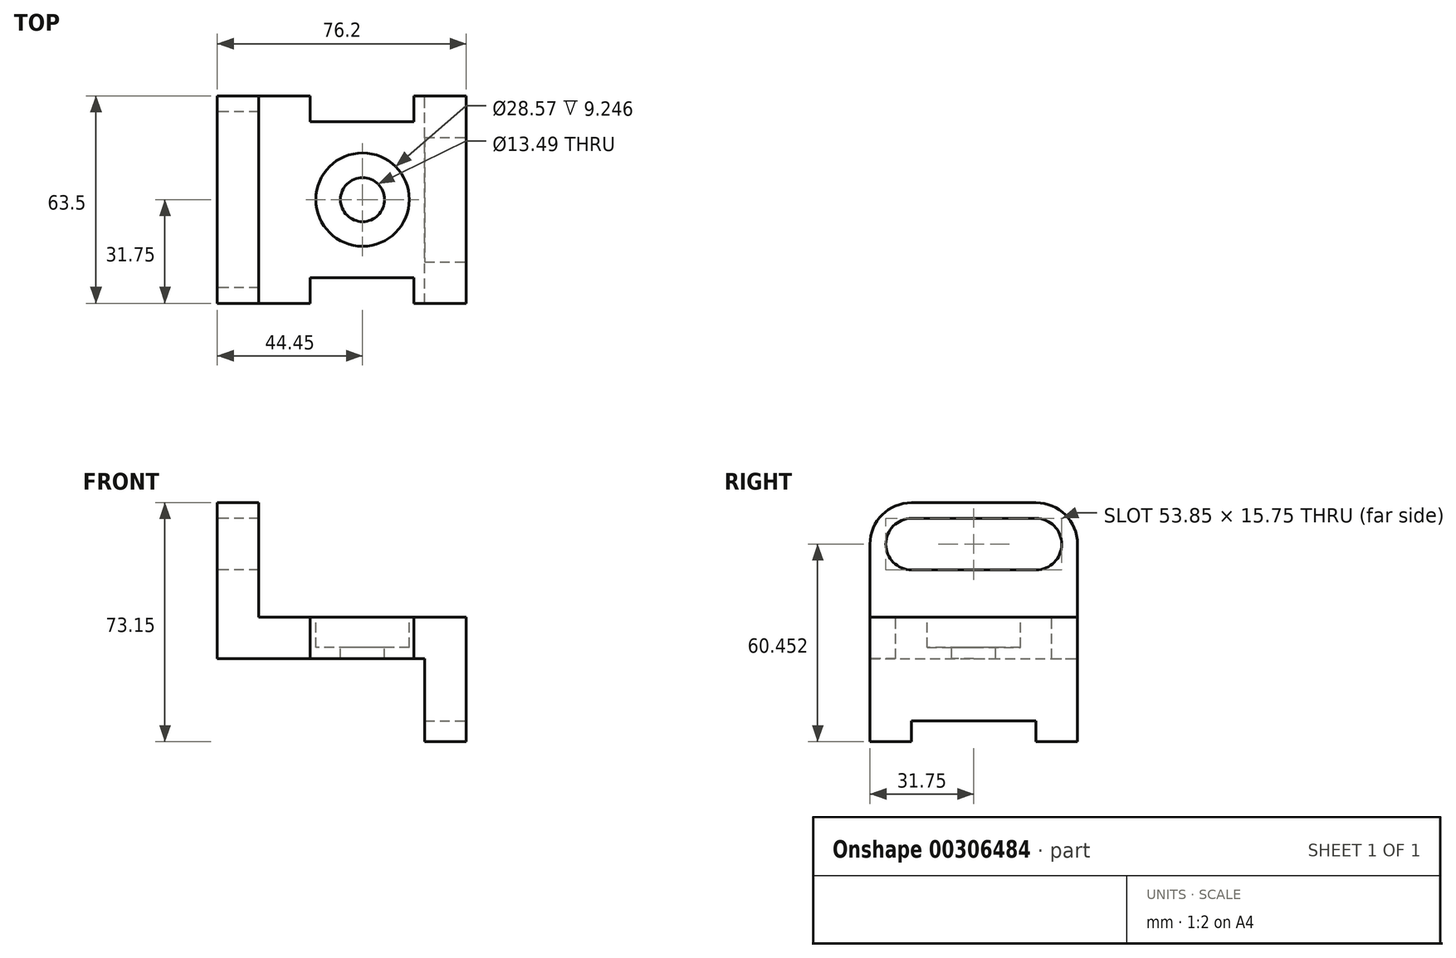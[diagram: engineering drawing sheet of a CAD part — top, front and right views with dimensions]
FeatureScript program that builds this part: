
annotation { "Feature Type Name" : "Feature", "Feature Type Description" : "" }
export const myFeature = defineFeature(function(context is Context, id is Id, definition is map)
    precondition{}
    {
        {
            var Q0;
            Q0=qCreatedBy(makeId("Front.planeOp"),FACE);
            var sketch = newSketch(context, id + "F0", { "sketchPlane" : qUnion([Q0])});
            skLineSegment(sketch, "E0", {"start": v(0, 12.7) * mm, "end": v(76.2, 12.7) * mm});
            skLineSegment(sketch, "E1", {"start": v(76.2, 12.7) * mm, "end": v(76.2, -25.4) * mm});
            skLineSegment(sketch, "E2", {"start": v(76.2, -25.4) * mm, "end": v(63.5, -25.4) * mm});
            skLineSegment(sketch, "E3", {"start": v(63.5, -25.4) * mm, "end": v(63.5, 0) * mm});
            skLineSegment(sketch, "E4", {"start": v(63.5, 0) * mm, "end": v(0, 0) * mm});
            skLineSegment(sketch, "E5", {"start": v(0, 12.7) * mm, "end": v(0, 0) * mm});
            skSolve(sketch);
        }
        {
            var Q0;
            Q0 = qSketchRegion(id + "F0", true);
            extrude(context, id + "F1", {"entities" : qUnion([Q0]), "depth" : 63.5 * mm});
        }
        {
            var Q0;
            Q0=makeQuery(id+"F1.opExtrude","SWEPT_FACE",FACE,{"disambiguationData":[OSD([sQuery(id+"F0.wireOp",EDGE,"E0")])]});
            var sketch = newSketch(context, id + "F2", { "sketchPlane" : qUnion([Q0])});
            skLineSegment(sketch, "E6.bottom", {"start": v(28.45, -63.5) * mm, "end": v(60.2, -63.5) * mm});
            skLineSegment(sketch, "E6.top", {"start": v(28.45, -55.63) * mm, "end": v(60.2, -55.63) * mm});
            skLineSegment(sketch, "E6.left", {"start": v(28.45, -63.5) * mm, "end": v(28.45, -55.63) * mm});
            skLineSegment(sketch, "E6.right", {"start": v(60.2, -63.5) * mm, "end": v(60.2, -55.63) * mm});
            skLineSegment(sketch, "E7.bottom", {"start": v(28.45, 0) * mm, "end": v(60.2, 0) * mm});
            skLineSegment(sketch, "E7.top", {"start": v(28.45, -7.87) * mm, "end": v(60.2, -7.87) * mm});
            skLineSegment(sketch, "E7.left", {"start": v(28.45, 0) * mm, "end": v(28.45, -7.87) * mm});
            skLineSegment(sketch, "E7.right", {"start": v(60.2, 0) * mm, "end": v(60.2, -7.87) * mm});
            skSolve(sketch);
        }
        {
            var Q0;
            Q0 = qSketchRegion(id + "F2", true);
            extrude(context, id + "F3", {"entities" : qUnion([Q0]), "operationType" : NewBodyOperationType.REMOVE, "endBound" : BoundingType.THROUGH_ALL, "oppositeDirection" : true, "depth" : 25.4 * mm});
        }
        {
            var Q0;
            Q0=makeQuery(id+"F1.opExtrude","SWEPT_FACE",FACE,{"disambiguationData":[OSD([sQuery(id+"F0.wireOp",EDGE,"E1")])]});
            var sketch = newSketch(context, id + "F4", { "sketchPlane" : qUnion([Q0])});
            skLineSegment(sketch, "E8.bottom", {"start": v(-50.8, -25.4) * mm, "end": v(-12.7, -25.4) * mm});
            skLineSegment(sketch, "E8.top", {"start": v(-50.8, -19.05) * mm, "end": v(-12.7, -19.05) * mm});
            skLineSegment(sketch, "E8.left", {"start": v(-50.8, -25.4) * mm, "end": v(-50.8, -19.05) * mm});
            skLineSegment(sketch, "E8.right", {"start": v(-12.7, -25.4) * mm, "end": v(-12.7, -19.05) * mm});
            skSolve(sketch);
        }
        {
            var Q0;
            Q0=makeQuery(id+"F4.imprint","IMPRINT",FACE,{"disambiguationData":[TD([[makeQuery(id+"F4.imprint","IMPRINT",EDGE,{"derivedFrom":sQuery(id+"F4.wireOp",EDGE,"E8.bottom")}),1.0]])]});
            extrude(context, id + "F5", {"entities" : qUnion([Q0]), "operationType" : NewBodyOperationType.REMOVE, "endBound" : BoundingType.THROUGH_ALL, "oppositeDirection" : true, "depth" : 25.4 * mm});
        }
        {
            var Q0;
            Q0=qCreatedBy(makeId("Right.planeOp"),FACE);
            var sketch = newSketch(context, id + "F6", { "sketchPlane" : qUnion([Q0])});
            skLineSegment(sketch, "E9", {"start": v(-63.5, 12.7) * mm, "end": v(-63.5, 35.05) * mm});
            skArc(sketch, "E10", {"start": v(-50.8, 47.75) * mm, "mid": v(-59.78, 44.03) * mm, "end": v(-63.5, 35.05) * mm});
            skLineSegment(sketch, "E11", {"start": v(-50.8, 47.75) * mm, "end": v(-31.75, 47.75) * mm});
            skLineSegment(sketch, "E12", {"start": v(-31.75, 47.75) * mm, "end": v(-31.75, 40.13) * mm, "construction": true});
            skArc(sketch, "E13.MirrorCS", {"start": v(-12.7, 47.75) * mm, "mid": v(-3.72, 44.03) * mm, "end": v(0, 35.05) * mm});
            skLineSegment(sketch, "E14.MirrorCS", {"start": v(0, 12.7) * mm, "end": v(0, 35.05) * mm});
            skLineSegment(sketch, "E15.MirrorCS", {"start": v(-12.7, 47.75) * mm, "end": v(-31.75, 47.75) * mm});
            skArc(sketch, "E16", {"start": v(-50.8, 42.93) * mm, "mid": v(-58.67, 35.05) * mm, "end": v(-50.8, 27.18) * mm});
            skArc(sketch, "E17", {"start": v(-12.7, 27.18) * mm, "mid": v(-4.83, 35.05) * mm, "end": v(-12.7, 42.93) * mm});
            skLineSegment(sketch, "E18", {"start": v(-50.8, 42.93) * mm, "end": v(-12.7, 42.93) * mm});
            skLineSegment(sketch, "E19", {"start": v(-50.8, 27.18) * mm, "end": v(-12.7, 27.18) * mm});
            skLineSegment(sketch, "E20", {"start": v(-63.5, 12.7) * mm, "end": v(0, 12.7) * mm});
            skSolve(sketch);
        }
        {
            var Q0;
            Q0 = qSketchRegion(id + "F6", true);
            extrude(context, id + "F7", {"entities" : qUnion([Q0]), "operationType" : NewBodyOperationType.ADD, "depth" : 12.7 * mm});
        }
        {
            var Q0;
            Q0=makeQuery(id+"F1.opExtrude","SWEPT_FACE",FACE,{"disambiguationData":[OSD([sQuery(id+"F0.wireOp",EDGE,"E0")])]});
            var sketch = newSketch(context, id + "F8", { "sketchPlane" : qUnion([Q0])});
            skCircle(sketch, "E21", {"center": v(44.45, -31.75) * mm, "radius": 14.29 * mm});
            skSolve(sketch);
        }
        {
            var Q0;
            Q0 = qSketchRegion(id + "F8", true);
            extrude(context, id + "F9", {"entities" : qUnion([Q0]), "operationType" : NewBodyOperationType.REMOVE, "oppositeDirection" : true, "depth" : 9.25 * mm});
        }
        {
            var Q0;
            Q0=makeQuery(id+"F9.boolean.opBoolean","COPY",FACE,{"derivedFrom":makeQuery(id+"F9.opExtrude","CAP_FACE",FACE,{"disambiguationData":[OSD([sQuery(id+"F8.wireOp",EDGE,"E21")])],"isStart":false})});
            var sketch = newSketch(context, id + "F10", { "sketchPlane" : qUnion([Q0])});
            skCircle(sketch, "E22", {"center": v(44.45, -31.75) * mm, "radius": 6.74 * mm});
            skSolve(sketch);
        }
        {
            var Q0;
            Q0 = qSketchRegion(id + "F10", true);
            extrude(context, id + "F11", {"entities" : qUnion([Q0]), "operationType" : NewBodyOperationType.REMOVE, "oppositeDirection" : true, "depth" : 25.4 * mm});
        }
    });
